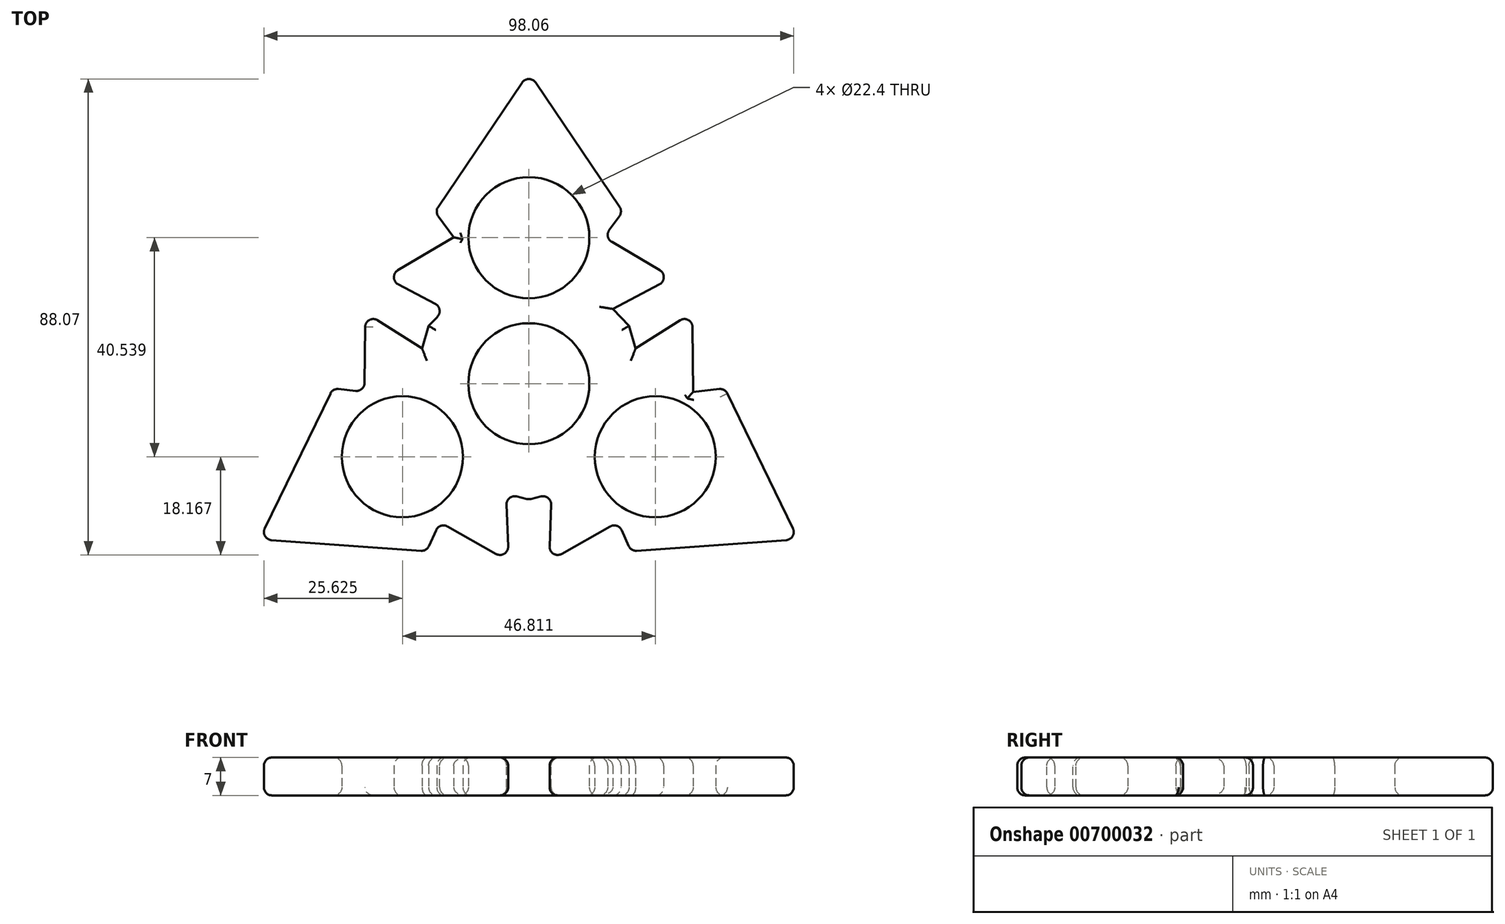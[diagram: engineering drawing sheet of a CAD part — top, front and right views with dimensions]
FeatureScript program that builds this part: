
annotation { "Feature Type Name" : "Feature", "Feature Type Description" : "" }
export const myFeature = defineFeature(function(context is Context, id is Id, definition is map)
    precondition{}
    {
        {
            var Q0;
            Q0=qCreatedBy(makeId("Top.planeOp"),FACE);
            var sketch = newSketch(context, id + "F0", { "sketchPlane" : qUnion([Q0])});
            skCircle(sketch, "E0", {"center": v(0, 0) * mm, "radius": 11.2 * mm});
            skLineSegment(sketch, "E1", {"start": v(-13.91, 27.1) * mm, "end": v(-17.39, 31.86) * mm});
            skLineSegment(sketch, "E2", {"start": v(-17.39, 31.86) * mm, "end": v(0, 57.56) * mm});
            skLineSegment(sketch, "E3.MirrorCS", {"start": v(17.39, 31.86) * mm, "end": v(0, 57.56) * mm});
            skLineSegment(sketch, "E4.MirrorCS", {"start": v(13.91, 27.1) * mm, "end": v(17.39, 31.86) * mm});
            skLineSegment(sketch, "E5", {"start": v(-13.91, 27.1) * mm, "end": v(-26.55, 19.64) * mm});
            skLineSegment(sketch, "E6", {"start": v(-26.55, 19.64) * mm, "end": v(-15.55, 13.84) * mm});
            skLineSegment(sketch, "E7", {"start": v(-15.55, 13.84) * mm, "end": v(-22.58, 6.5) * mm});
            skLineSegment(sketch, "E8", {"start": v(-22.58, 6.5) * mm, "end": v(-13.2, 0) * mm});
            skLineSegment(sketch, "E9.MirrorCS", {"start": v(13.91, 27.1) * mm, "end": v(26.55, 19.64) * mm});
            skLineSegment(sketch, "E10.MirrorCS", {"start": v(26.55, 19.64) * mm, "end": v(15.55, 13.84) * mm});
            skLineSegment(sketch, "E11.MirrorCS", {"start": v(15.55, 13.84) * mm, "end": v(22.58, 6.5) * mm});
            skLineSegment(sketch, "E12.MirrorCS", {"start": v(22.58, 6.5) * mm, "end": v(13.2, 0) * mm});
            skCircle(sketch, "E13", {"center": v(0, 27.03) * mm, "radius": 11.2 * mm});
            skCircle(sketch, "E14.1.1", {"center": v(-23.4, -13.51) * mm, "radius": 11.2 * mm});
            skLineSegment(sketch, "E14.1.2", {"start": v(-36.28, -0.87) * mm, "end": v(-49.85, -28.78) * mm});
            skLineSegment(sketch, "E14.1.3", {"start": v(-18.9, -30.98) * mm, "end": v(-49.85, -28.78) * mm});
            skLineSegment(sketch, "E14.1.4", {"start": v(-30.42, -1.5) * mm, "end": v(-30.28, 13.17) * mm});
            skLineSegment(sketch, "E14.1.5", {"start": v(-30.28, 13.17) * mm, "end": v(-19.76, 6.55) * mm});
            skLineSegment(sketch, "E14.1.6", {"start": v(-19.76, 6.55) * mm, "end": v(-16.92, 16.3) * mm});
            skLineSegment(sketch, "E14.1.7", {"start": v(-16.92, 16.3) * mm, "end": v(-6.6, 11.43) * mm});
            skLineSegment(sketch, "E14.1.8", {"start": v(5.65, -22.8) * mm, "end": v(6.6, -11.43) * mm});
            skLineSegment(sketch, "E14.1.9", {"start": v(-4.2, -20.39) * mm, "end": v(5.65, -22.8) * mm});
            skLineSegment(sketch, "E14.1.10", {"start": v(-3.74, -32.8) * mm, "end": v(-4.2, -20.39) * mm});
            skLineSegment(sketch, "E14.1.11", {"start": v(-16.5, -25.6) * mm, "end": v(-3.74, -32.8) * mm});
            skCircle(sketch, "E14.2.1", {"center": v(23.4, -13.51) * mm, "radius": 11.2 * mm});
            skLineSegment(sketch, "E14.2.2", {"start": v(18.9, -30.98) * mm, "end": v(49.85, -28.78) * mm});
            skLineSegment(sketch, "E14.2.3", {"start": v(36.28, -0.87) * mm, "end": v(49.85, -28.78) * mm});
            skLineSegment(sketch, "E14.2.4", {"start": v(16.5, -25.6) * mm, "end": v(3.74, -32.8) * mm});
            skLineSegment(sketch, "E14.2.5", {"start": v(3.74, -32.8) * mm, "end": v(4.2, -20.39) * mm});
            skLineSegment(sketch, "E14.2.6", {"start": v(4.2, -20.39) * mm, "end": v(-5.65, -22.8) * mm});
            skLineSegment(sketch, "E14.2.7", {"start": v(-5.65, -22.8) * mm, "end": v(-6.6, -11.43) * mm});
            skLineSegment(sketch, "E14.2.8", {"start": v(16.92, 16.3) * mm, "end": v(6.6, 11.43) * mm});
            skLineSegment(sketch, "E14.2.9", {"start": v(19.76, 6.55) * mm, "end": v(16.92, 16.3) * mm});
            skLineSegment(sketch, "E14.2.10", {"start": v(30.28, 13.17) * mm, "end": v(19.76, 6.55) * mm});
            skLineSegment(sketch, "E14.2.11", {"start": v(30.42, -1.5) * mm, "end": v(30.28, 13.17) * mm});
            skLineSegment(sketch, "E15", {"start": v(-36.28, -0.87) * mm, "end": v(-30.42, -1.5) * mm});
            skLineSegment(sketch, "E16", {"start": v(-18.9, -30.98) * mm, "end": v(-16.5, -25.6) * mm});
            skLineSegment(sketch, "E17", {"start": v(16.5, -25.6) * mm, "end": v(18.9, -30.98) * mm});
            skLineSegment(sketch, "E18", {"start": v(36.28, -0.87) * mm, "end": v(30.42, -1.5) * mm});
            skSolve(sketch);
        }
        {
            var Q0;
            Q0=makeQuery(id+"F0.imprint","IMPRINT",FACE,{"disambiguationData":[TD([[makeQuery(id+"F0.imprint","IMPRINT",EDGE,{"derivedFrom":sQuery(id+"F0.wireOp",EDGE,"E0")}),-1.0]])]});
            extrude(context, id + "F1", {"entities" : qUnion([Q0]), "depth" : 7 * mm, "offsetDistance" : 25 * mm});
        }
        {
            var Q0;
            Q0=makeQuery(id+"F1.opExtrude","CAP_FACE",FACE,{"disambiguationData":[OSD([sQuery(id+"F0.wireOp",EDGE,"E0"),sQuery(id+"F0.wireOp",EDGE,"E1"),sQuery(id+"F0.wireOp",EDGE,"E2"),sQuery(id+"F0.wireOp",EDGE,"E3.MirrorCS"),sQuery(id+"F0.wireOp",EDGE,"E4.MirrorCS"),sQuery(id+"F0.wireOp",EDGE,"E5"),sQuery(id+"F0.wireOp",EDGE,"E6"),sQuery(id+"F0.wireOp",EDGE,"E7"),sQuery(id+"F0.wireOp",EDGE,"E9.MirrorCS"),sQuery(id+"F0.wireOp",EDGE,"E10.MirrorCS"),sQuery(id+"F0.wireOp",EDGE,"E11.MirrorCS"),sQuery(id+"F0.wireOp",EDGE,"E13"),sQuery(id+"F0.wireOp",EDGE,"E14.1.1"),sQuery(id+"F0.wireOp",EDGE,"E14.1.2"),sQuery(id+"F0.wireOp",EDGE,"E14.1.3"),sQuery(id+"F0.wireOp",EDGE,"E14.1.4"),sQuery(id+"F0.wireOp",EDGE,"E14.1.5"),sQuery(id+"F0.wireOp",EDGE,"E14.1.6"),sQuery(id+"F0.wireOp",EDGE,"E14.1.9"),sQuery(id+"F0.wireOp",EDGE,"E14.1.10"),sQuery(id+"F0.wireOp",EDGE,"E14.1.11"),sQuery(id+"F0.wireOp",EDGE,"E14.2.1"),sQuery(id+"F0.wireOp",EDGE,"E14.2.2"),sQuery(id+"F0.wireOp",EDGE,"E14.2.3"),sQuery(id+"F0.wireOp",EDGE,"E14.2.4"),sQuery(id+"F0.wireOp",EDGE,"E14.2.5"),sQuery(id+"F0.wireOp",EDGE,"E14.2.6"),sQuery(id+"F0.wireOp",EDGE,"E14.2.9"),sQuery(id+"F0.wireOp",EDGE,"E14.2.10"),sQuery(id+"F0.wireOp",EDGE,"E14.2.11"),sQuery(id+"F0.wireOp",EDGE,"E15"),sQuery(id+"F0.wireOp",EDGE,"E16"),sQuery(id+"F0.wireOp",EDGE,"E17"),sQuery(id+"F0.wireOp",EDGE,"E18")])],"isStart":false});
            var Q1;
            Q1=makeQuery(id+"F1.opExtrude","CAP_FACE",FACE,{"disambiguationData":[OSD([sQuery(id+"F0.wireOp",EDGE,"E0"),sQuery(id+"F0.wireOp",EDGE,"E1"),sQuery(id+"F0.wireOp",EDGE,"E2"),sQuery(id+"F0.wireOp",EDGE,"E3.MirrorCS"),sQuery(id+"F0.wireOp",EDGE,"E4.MirrorCS"),sQuery(id+"F0.wireOp",EDGE,"E5"),sQuery(id+"F0.wireOp",EDGE,"E6"),sQuery(id+"F0.wireOp",EDGE,"E7"),sQuery(id+"F0.wireOp",EDGE,"E9.MirrorCS"),sQuery(id+"F0.wireOp",EDGE,"E10.MirrorCS"),sQuery(id+"F0.wireOp",EDGE,"E11.MirrorCS"),sQuery(id+"F0.wireOp",EDGE,"E13"),sQuery(id+"F0.wireOp",EDGE,"E14.1.1"),sQuery(id+"F0.wireOp",EDGE,"E14.1.2"),sQuery(id+"F0.wireOp",EDGE,"E14.1.3"),sQuery(id+"F0.wireOp",EDGE,"E14.1.4"),sQuery(id+"F0.wireOp",EDGE,"E14.1.5"),sQuery(id+"F0.wireOp",EDGE,"E14.1.6"),sQuery(id+"F0.wireOp",EDGE,"E14.1.9"),sQuery(id+"F0.wireOp",EDGE,"E14.1.10"),sQuery(id+"F0.wireOp",EDGE,"E14.1.11"),sQuery(id+"F0.wireOp",EDGE,"E14.2.1"),sQuery(id+"F0.wireOp",EDGE,"E14.2.2"),sQuery(id+"F0.wireOp",EDGE,"E14.2.3"),sQuery(id+"F0.wireOp",EDGE,"E14.2.4"),sQuery(id+"F0.wireOp",EDGE,"E14.2.5"),sQuery(id+"F0.wireOp",EDGE,"E14.2.6"),sQuery(id+"F0.wireOp",EDGE,"E14.2.9"),sQuery(id+"F0.wireOp",EDGE,"E14.2.10"),sQuery(id+"F0.wireOp",EDGE,"E14.2.11"),sQuery(id+"F0.wireOp",EDGE,"E15"),sQuery(id+"F0.wireOp",EDGE,"E16"),sQuery(id+"F0.wireOp",EDGE,"E17"),sQuery(id+"F0.wireOp",EDGE,"E18")])],"isStart":true});
            var Q2;
            Q2=makeQuery(id+"F1.opExtrude","SWEPT_FACE",FACE,{"disambiguationData":[OSD([sQuery(id+"F0.wireOp",EDGE,"E14.2.2")])]});
            var Q3;
            Q3=makeQuery(id+"F1.opExtrude","SWEPT_FACE",FACE,{"disambiguationData":[OSD([sQuery(id+"F0.wireOp",EDGE,"E14.2.4")])]});
            var Q4;
            Q4=makeQuery(id+"F1.opExtrude","SWEPT_EDGE",EDGE,{"disambiguationData":[OSD([sQuery(id+"F0.wireOp",EDGE,"E14.2.2"),sQuery(id+"F0.wireOp",EDGE,"E17")])]});
            var Q5;
            Q5=makeQuery(id+"F1.opExtrude","SWEPT_FACE",FACE,{"disambiguationData":[OSD([sQuery(id+"F0.wireOp",EDGE,"E14.1.9")])]});
            var Q6;
            Q6=makeQuery(id+"F1.opExtrude","SWEPT_EDGE",EDGE,{"disambiguationData":[OSD([sQuery(id+"F0.wireOp",EDGE,"E14.2.4"),sQuery(id+"F0.wireOp",EDGE,"E14.2.5")])]});
            var Q7;
            Q7=makeQuery(id+"F1.opExtrude","SWEPT_FACE",FACE,{"disambiguationData":[OSD([sQuery(id+"F0.wireOp",EDGE,"E14.2.6")])]});
            var Q8;
            Q8=makeQuery(id+"F1.opExtrude","SWEPT_FACE",FACE,{"disambiguationData":[OSD([sQuery(id+"F0.wireOp",EDGE,"E14.1.11")])]});
            var Q9;
            Q9=makeQuery(id+"F1.opExtrude","SWEPT_EDGE",EDGE,{"disambiguationData":[OSD([sQuery(id+"F0.wireOp",EDGE,"E14.1.3"),sQuery(id+"F0.wireOp",EDGE,"E16")])]});
            var Q10;
            Q10=makeQuery(id+"F1.opExtrude","SWEPT_FACE",FACE,{"disambiguationData":[OSD([sQuery(id+"F0.wireOp",EDGE,"E17")])]});
            var Q11;
            Q11=makeQuery(id+"F1.opExtrude","SWEPT_FACE",FACE,{"disambiguationData":[OSD([sQuery(id+"F0.wireOp",EDGE,"E14.2.5")])]});
            var Q12;
            Q12=makeQuery(id+"F1.opExtrude","SWEPT_FACE",FACE,{"disambiguationData":[OSD([sQuery(id+"F0.wireOp",EDGE,"E9.MirrorCS")])]});
            var Q13;
            Q13=makeQuery(id+"F1.opExtrude","SWEPT_EDGE",EDGE,{"disambiguationData":[OSD([sQuery(id+"F0.wireOp",EDGE,"E14.2.10"),sQuery(id+"F0.wireOp",EDGE,"E14.2.11")])]});
            var Q14;
            Q14=makeQuery(id+"F1.opExtrude","SWEPT_EDGE",EDGE,{"disambiguationData":[OSD([sQuery(id+"F0.wireOp",EDGE,"E14.2.3"),sQuery(id+"F0.wireOp",EDGE,"E18")])]});
            var Q15;
            Q15=makeQuery(id+"F1.opExtrude","SWEPT_FACE",FACE,{"disambiguationData":[OSD([sQuery(id+"F0.wireOp",EDGE,"E14.1.2")])]});
            var Q16;
            Q16=makeQuery(id+"F1.opExtrude","SWEPT_FACE",FACE,{"disambiguationData":[OSD([sQuery(id+"F0.wireOp",EDGE,"E14.1.4")])]});
            var Q17;
            Q17=makeQuery(id+"F1.opExtrude","SWEPT_FACE",FACE,{"disambiguationData":[OSD([sQuery(id+"F0.wireOp",EDGE,"E6")])]});
            var Q18;
            Q18=makeQuery(id+"F1.opExtrude","SWEPT_EDGE",EDGE,{"disambiguationData":[OSD([sQuery(id+"F0.wireOp",EDGE,"E1"),sQuery(id+"F0.wireOp",EDGE,"E2")])]});
            var Q19;
            Q19=makeQuery(id+"F1.opExtrude","SWEPT_FACE",FACE,{"disambiguationData":[OSD([sQuery(id+"F0.wireOp",EDGE,"E2")])]});
            var Q20;
            Q20=makeQuery(id+"F1.opExtrude","SWEPT_FACE",FACE,{"disambiguationData":[OSD([sQuery(id+"F0.wireOp",EDGE,"E14.1.3")])]});
            var Q21;
            Q21=makeQuery(id+"F1.opExtrude","SWEPT_FACE",FACE,{"disambiguationData":[OSD([sQuery(id+"F0.wireOp",EDGE,"E14.1.10")])]});
            var Q22;
            Q22=makeQuery(id+"F1.opExtrude","SWEPT_FACE",FACE,{"disambiguationData":[OSD([sQuery(id+"F0.wireOp",EDGE,"E4.MirrorCS")])]});
            var Q23;
            Q23=makeQuery(id+"F1.opExtrude","SWEPT_EDGE",EDGE,{"disambiguationData":[OSD([sQuery(id+"F0.wireOp",EDGE,"E14.1.4"),sQuery(id+"F0.wireOp",EDGE,"E14.1.5")])]});
            fillet(context, id + "F2", {"entities" : qUnion([Q0, Q1, Q2, Q3, Q4, Q5, Q6, Q7, Q8, Q9, Q10, Q11, Q12, Q13, Q14, Q15, Q16, Q17, Q18, Q19, Q20, Q21, Q22, Q23]), "radius" : 1.5 * mm, "tangentPropagation" : true, "allowEdgeOverflow" : false});
        }
    });
